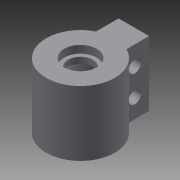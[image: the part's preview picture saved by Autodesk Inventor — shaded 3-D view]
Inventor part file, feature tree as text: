
AUTODESK INVENTOR PART (.ipt)
format: ipt  version: 2013 SP2 (Build 170200200, 200)  size: 127,488 bytes
history: native  units: mm
features: extrude x2, sketch x2, revolve x1
ambient origin geometry x8: Origin, YZ Plane, XZ Plane, XY Plane, X Axis, Y Axis, Z Axis, Center Point
bodies: Solid1 (feature_tree)
feature tree (5):
  revolve  "Revolution1"  Angle=90.0deg
  extrude  "Extrusion1"  TaperAngle=0.0deg  [1 undecoded]
  extrude  "Extrusion2"  Depth=2.0mm
  sketch  "Sketch3"  dims[d2=15.0mm d7=90.0deg]
  sketch  "Sketch4"  dims[d12=2.0mm d14=0.0mm d16=2.0mm d17=4.25mm d20=8.0mm d21=0.0mm d28=14.0mm d29=3.2mm d30=3.2mm d31=7.0mm d32=10.0mm d33=0.0mm d34=3.75mm d35=20.071286mm d36=9.0mm d37=2.5mm d39=1.0mm d40=5.0mm d41=7.163077mm d42=3.25mm d43=1.60838mm d44=8.39162mm]
note: 1 required parameter value undecoded (feature->parameter linkage not recoverable at this tier; creation-order binding heuristic only, values carry confidence <= 0.55)
